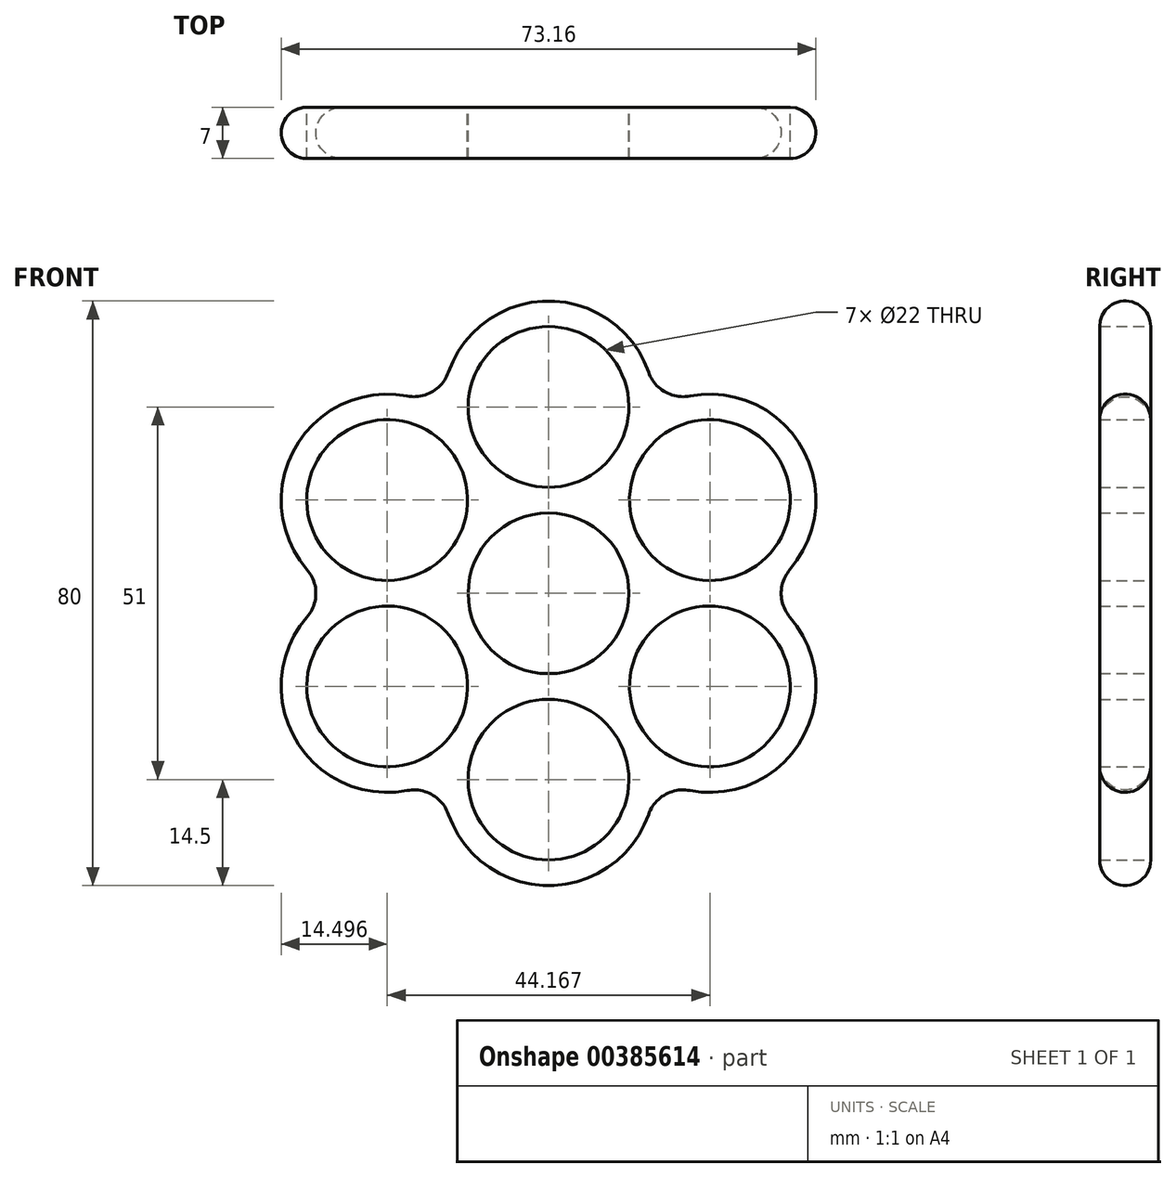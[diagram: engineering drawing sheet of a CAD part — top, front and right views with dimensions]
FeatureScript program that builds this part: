
annotation { "Feature Type Name" : "Feature", "Feature Type Description" : "" }
export const myFeature = defineFeature(function(context is Context, id is Id, definition is map)
    precondition{}
    {
        {
            var Q0;
            Q0=qCreatedBy(makeId("Front.planeOp"),FACE);
            var sketch = newSketch(context, id + "F0", { "sketchPlane" : qUnion([Q0])});
            skCircle(sketch, "E0", {"center": v(0, 0) * mm, "radius": 11 * mm});
            skCircle(sketch, "E1", {"center": v(0, 25.5) * mm, "radius": 11 * mm});
            skCircle(sketch, "E2.1.0", {"center": v(-22.08, 12.75) * mm, "radius": 11 * mm});
            skArc(sketch, "E2.1.1", {"start": v(-19.36, 27) * mm, "mid": v(-34.64, 20) * mm, "end": v(-33.05, 3.27) * mm});
            skCircle(sketch, "E2.2.0", {"center": v(-22.08, -12.75) * mm, "radius": 11 * mm});
            skArc(sketch, "E2.2.1", {"start": v(-33.05, -3.27) * mm, "mid": v(-34.64, -20) * mm, "end": v(-19.36, -27) * mm});
            skCircle(sketch, "E2.3.0", {"center": v(0, -25.5) * mm, "radius": 11 * mm});
            skCircle(sketch, "E2.4.0", {"center": v(22.08, -12.75) * mm, "radius": 11 * mm});
            skArc(sketch, "E2.4.1", {"start": v(19.36, -27) * mm, "mid": v(34.64, -20) * mm, "end": v(33.05, -3.27) * mm});
            skCircle(sketch, "E2.5.0", {"center": v(22.08, 12.75) * mm, "radius": 11 * mm});
            skArc(sketch, "E3.trimOffspring", {"start": v(-13.7, -30.26) * mm, "mid": v(0, -40) * mm, "end": v(13.7, -30.26) * mm});
            skArc(sketch, "E4.trimOffspring", {"start": v(33.05, 3.27) * mm, "mid": v(34.64, 20) * mm, "end": v(19.36, 27) * mm});
            skArc(sketch, "E5.trimOffspring", {"start": v(13.7, 30.26) * mm, "mid": v(0, 40) * mm, "end": v(-13.7, 30.26) * mm});
            skPoint(sketch, "E6.visualSharp", {"position": v(-14.5, 25.1) * mm});
            skArc(sketch, "E6.filletArc", {"start": v(-19.36, 27) * mm, "mid": v(-15.92, 27.57) * mm, "end": v(-13.7, 30.26) * mm});
            skPoint(sketch, "E7.visualSharp", {"position": v(14.5, 25.1) * mm});
            skArc(sketch, "E7.filletArc", {"start": v(13.7, 30.26) * mm, "mid": v(15.92, 27.57) * mm, "end": v(19.36, 27) * mm});
            skPoint(sketch, "E8.visualSharp", {"position": v(28.99, 0) * mm});
            skArc(sketch, "E8.filletArc", {"start": v(33.05, 3.27) * mm, "mid": v(31.84, 0) * mm, "end": v(33.05, -3.27) * mm});
            skPoint(sketch, "E9.visualSharp", {"position": v(-28.99, 0) * mm});
            skArc(sketch, "E9.filletArc", {"start": v(-33.05, -3.27) * mm, "mid": v(-31.84, 0) * mm, "end": v(-33.05, 3.27) * mm});
            skPoint(sketch, "E10.visualSharp", {"position": v(-14.5, -25.1) * mm});
            skArc(sketch, "E10.filletArc", {"start": v(-13.7, -30.26) * mm, "mid": v(-15.92, -27.57) * mm, "end": v(-19.36, -27) * mm});
            skPoint(sketch, "E11.visualSharp", {"position": v(14.5, -25.1) * mm});
            skArc(sketch, "E11.filletArc", {"start": v(19.36, -27) * mm, "mid": v(15.92, -27.57) * mm, "end": v(13.7, -30.26) * mm});
            skSolve(sketch);
        }
        {
            var Q0;
            Q0=makeQuery(id+"F0.imprint","IMPRINT",FACE,{"disambiguationData":[TD([[makeQuery(id+"F0.imprint","IMPRINT",EDGE,{"derivedFrom":sQuery(id+"F0.wireOp",EDGE,"E0")}),-1.0]])]});
            extrude(context, id + "F1", {"entities" : qUnion([Q0]), "depth" : 7 * mm, "offsetDistance" : 25 * mm});
        }
        {
            var Q0;
            Q0=makeQuery(id+"F1.opExtrude","CAP_EDGE",EDGE,{"disambiguationData":[OSD([sQuery(id+"F0.wireOp",EDGE,"E5.trimOffspring")])],"isStart":false});
            var Q1;
            Q1=makeQuery(id+"F1.opExtrude","CAP_EDGE",EDGE,{"disambiguationData":[OSD([sQuery(id+"F0.wireOp",EDGE,"E5.trimOffspring")])],"isStart":true});
            fillet(context, id + "F2", {"entities" : qUnion([Q0, Q1]), "radius" : 3.5 * mm, "tangentPropagation" : true, "allowEdgeOverflow" : false});
        }
    });
